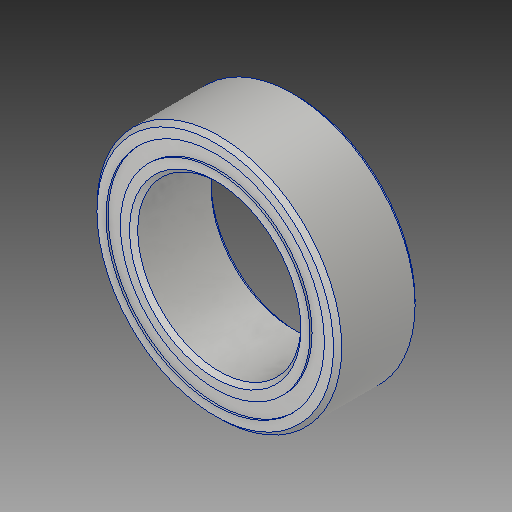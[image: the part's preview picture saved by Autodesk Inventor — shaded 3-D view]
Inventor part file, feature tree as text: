
AUTODESK INVENTOR PART (.ipt)
format: ipt  version: 2017 (Build 210142000, 142)  size: 611,328 bytes
history: native  units: in
note: dims shown in document units (in); Inventor stores cm internally (conversion verified against a paired STEP export)
features: other x11, revolve x5
ambient origin geometry x8: Origin, YZ Plane, XZ Plane, XY Plane, X Axis, Y Axis, Z Axis, Center Point
bodies: Solid1 (feature_tree), Solid2 (feature_tree), Solid3 (feature_tree), Solid4 (feature_tree), Solid5 (feature_tree), Solid6 (feature_tree), Solid7 (feature_tree), Solid8 (feature_tree), Solid9 (feature_tree), Solid10 (feature_tree), Solid11 (feature_tree), Solid12 (feature_tree), Solid13 (feature_tree), Solid14 (feature_tree), Solid15 (feature_tree), Solid16 (feature_tree)
feature tree (16):
  revolve  "Revolve1"  [1 undecoded]
  revolve  "Revolve3"  [1 undecoded]
  revolve  "Revolve4"  [1 undecoded]
  other  "CirPattern1[1]"
  other  "CirPattern1[2]"
  other  "CirPattern1[3]"
  other  "CirPattern1[4]"
  other  "CirPattern1[5]"
  other  "CirPattern1[6]"
  other  "CirPattern1[7]"
  other  "CirPattern1[8]"
  other  "CirPattern1[9]"
  other  "CirPattern1[10]"
  other  "CirPattern1[11]"
  revolve  "Revolve5[1]"  [1 undecoded]
  revolve  "Revolve5[2]"  [1 undecoded]
note: 5 required parameter values undecoded (feature->parameter linkage not recoverable at this tier; creation-order binding heuristic only, values carry confidence <= 0.55)
